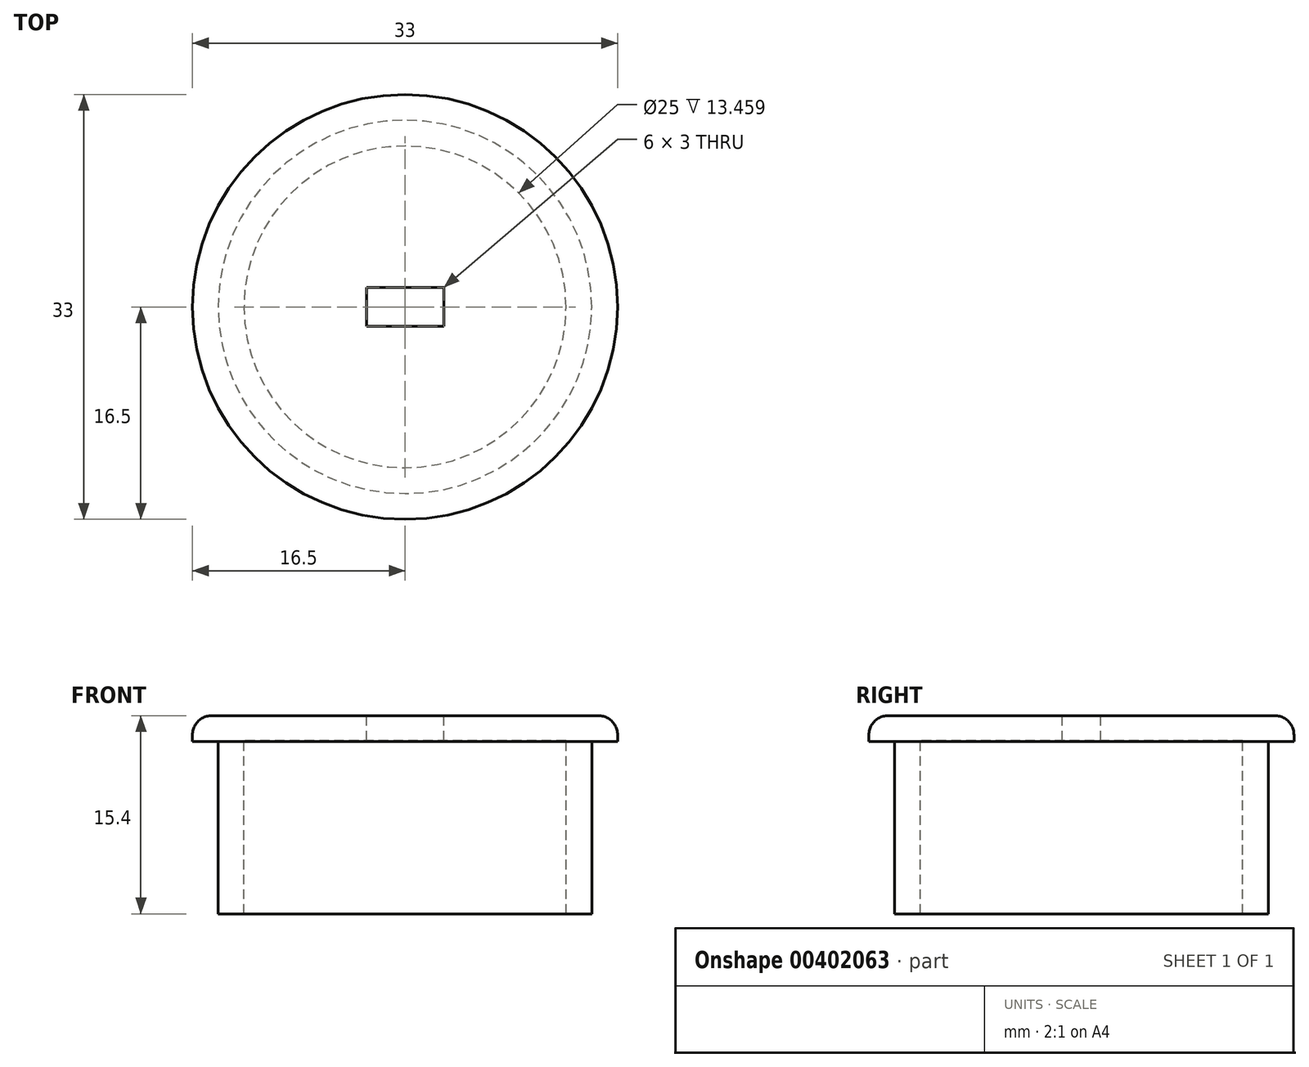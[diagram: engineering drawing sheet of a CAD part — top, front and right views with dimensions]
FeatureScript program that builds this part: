
annotation { "Feature Type Name" : "Feature", "Feature Type Description" : "" }
export const myFeature = defineFeature(function(context is Context, id is Id, definition is map)
    precondition{}
    {
        {
            var Q0;
            Q0=qCreatedBy(makeId("Front.planeOp"),FACE);
            var sketch = newSketch(context, id + "F0", { "sketchPlane" : qUnion([Q0])});
            skLineSegment(sketch, "E0", {"start": v(-14.5, 2) * mm, "end": v(-16.5, 2) * mm});
            skLineSegment(sketch, "E1", {"start": v(-16.5, 2) * mm, "end": v(-16.5, 4) * mm});
            skLineSegment(sketch, "E2", {"start": v(-16.5, 4) * mm, "end": v(0, 4) * mm});
            skLineSegment(sketch, "E3", {"start": v(0, 4) * mm, "end": v(0, 2.06) * mm});
            skLineSegment(sketch, "E4", {"start": v(-14.5, -11.4) * mm, "end": v(-12.5, -11.4) * mm});
            skLineSegment(sketch, "E5", {"start": v(-12.5, -11.4) * mm, "end": v(-12.5, 2.06) * mm});
            skLineSegment(sketch, "E6", {"start": v(-12.5, 2.06) * mm, "end": v(0, 2.06) * mm});
            skLineSegment(sketch, "E7", {"start": v(-14.5, 2) * mm, "end": v(-14.5, -11.4) * mm});
            skLineSegment(sketch, "E8", {"start": v(0, 2.06) * mm, "end": v(0, -18.08) * mm, "construction": true});
            skSolve(sketch);
        }
        {
            var Q0;
            Q0 = qSketchRegion(id + "F0", true);
            var Q1;
            Q1=sQuery(id+"F0.wireOp",EDGE,"E8");
            revolve(context, id + "F1", {"entities" : qUnion([Q0]), "axis" : qUnion([Q1]), "revolveType" : RevolveType.FULL});
        }
        {
            var Q0;
            Q0=makeQuery(id+"F1.opRevolve","SWEPT_FACE",FACE,{"disambiguationData":[OSD([sQuery(id+"F0.wireOp",EDGE,"E2")])]});
            var sketch = newSketch(context, id + "F2", { "sketchPlane" : qUnion([Q0])});
            skLineSegment(sketch, "E9.bottom", {"start": v(3, 1.5) * mm, "end": v(-3, 1.5) * mm});
            skLineSegment(sketch, "E9.top", {"start": v(3, -1.5) * mm, "end": v(-3, -1.5) * mm});
            skLineSegment(sketch, "E9.left", {"start": v(3, 1.5) * mm, "end": v(3, -1.5) * mm});
            skLineSegment(sketch, "E9.right", {"start": v(-3, 1.5) * mm, "end": v(-3, -1.5) * mm});
            skPoint(sketch, "E9.middle", {"position": v(0, 0) * mm});
            skSolve(sketch);
        }
        {
            var Q0;
            Q0 = qSketchRegion(id + "F2", true);
            extrude(context, id + "F3", {"entities" : qUnion([Q0]), "operationType" : NewBodyOperationType.REMOVE, "oppositeDirection" : true, "depth" : 25 * mm});
        }
        {
            var Q0;
            Q0=makeQuery(id+"F1.opRevolve","SWEPT_EDGE",EDGE,{"disambiguationData":[OSD([sQuery(id+"F0.wireOp",EDGE,"E1"),sQuery(id+"F0.wireOp",EDGE,"E2")])]});
            fillet(context, id + "F4", {"entities" : qUnion([Q0]), "radius" : 1.5 * mm, "tangentPropagation" : true, "allowEdgeOverflow" : false});
        }
    });
